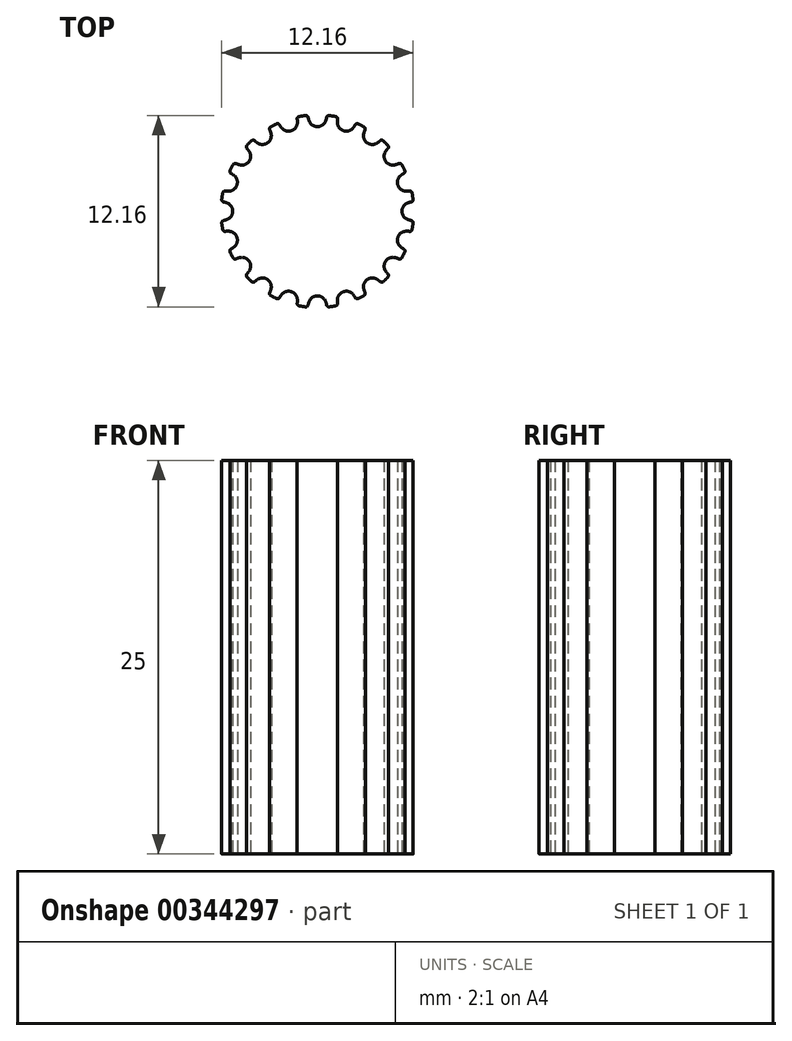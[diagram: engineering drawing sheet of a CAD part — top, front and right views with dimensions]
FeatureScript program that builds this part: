
annotation { "Feature Type Name" : "Feature", "Feature Type Description" : "" }
export const myFeature = defineFeature(function(context is Context, id is Id, definition is map)
    precondition{}
    {
        {
            var Q0;
            Q0=qCreatedBy(makeId("Top.planeOp"),FACE);
            var sketch = newSketch(context, id + "F0", { "sketchPlane" : qUnion([Q0])});
            skLineSegment(sketch, "E0", {"start": v(0, 6.12) * mm, "end": v(0, 6.37) * mm});
            skArc(sketch, "E1", {"start": v(-0.59, 5.95) * mm, "mid": v(-0.64, 6.05) * mm, "end": v(-0.75, 6.08) * mm});
            skArc(sketch, "E2", {"start": v(0.5, 5.7) * mm, "mid": v(0.56, 5.82) * mm, "end": v(0.59, 5.95) * mm});
            skLineSegment(sketch, "E3", {"start": v(0, 6.37) * mm, "end": v(0, 0) * mm, "construction": true});
            skCircle(sketch, "E4", {"center": v(0, 0) * mm, "radius": 6.12 * mm, "construction": true});
            skArc(sketch, "E5.trimOffspring", {"start": v(0.75, 6.08) * mm, "mid": v(0.64, 6.05) * mm, "end": v(0.59, 5.95) * mm});
            skArc(sketch, "E6.trimOffspring", {"start": v(-0.5, 5.7) * mm, "mid": v(0, 5.37) * mm, "end": v(0.5, 5.7) * mm});
            skArc(sketch, "E7.trimOffspring", {"start": v(-0.59, 5.95) * mm, "mid": v(-0.56, 5.82) * mm, "end": v(-0.5, 5.7) * mm});
            skPoint(sketch, "E8", {"position": v(0, 5.37) * mm});
            skCircle(sketch, "E9", {"center": v(0, 0) * mm, "radius": 6.37 * mm, "construction": true});
            skPoint(sketch, "E10", {"position": v(-0.96, 6.05) * mm});
            skPoint(sketch, "E11", {"position": v(0.96, 6.05) * mm});
            skArc(sketch, "E12", {"start": v(-0.75, 6.08) * mm, "mid": v(-0.86, 6.06) * mm, "end": v(-0.96, 6.05) * mm});
            skLineSegment(sketch, "E13", {"start": v(0, 0) * mm, "end": v(-1, 6.3) * mm, "construction": true});
            skLineSegment(sketch, "E14", {"start": v(0, 0) * mm, "end": v(1, 6.3) * mm, "construction": true});
            skArc(sketch, "E15", {"start": v(0.96, 6.05) * mm, "mid": v(0.86, 6.06) * mm, "end": v(0.75, 6.08) * mm});
            skLineSegment(sketch, "E16.1.0", {"start": v(0, 0) * mm, "end": v(0, 6.37) * mm, "construction": true});
            skLineSegment(sketch, "E17.2.3.0", {"start": v(0, 0) * mm, "end": v(-1.97, 6.06) * mm, "construction": true});
            skLineSegment(sketch, "E17.2.4.0", {"start": v(0, 0) * mm, "end": v(-2.9, 5.68) * mm, "construction": true});
            skLineSegment(sketch, "E17.2.5.0", {"start": v(0, 0) * mm, "end": v(-3.75, 5.16) * mm, "construction": true});
            skLineSegment(sketch, "E17.2.6.0", {"start": v(0, 0) * mm, "end": v(-4.5, 4.5) * mm, "construction": true});
            skLineSegment(sketch, "E17.2.7.0", {"start": v(0, 0) * mm, "end": v(-5.16, 3.75) * mm, "construction": true});
            skLineSegment(sketch, "E17.2.8.0", {"start": v(0, 0) * mm, "end": v(-5.68, 2.9) * mm, "construction": true});
            skLineSegment(sketch, "E17.2.9.0", {"start": v(0, 0) * mm, "end": v(-6.06, 1.97) * mm, "construction": true});
            skLineSegment(sketch, "E17.2.10.0", {"start": v(0, 0) * mm, "end": v(-6.3, 1) * mm, "construction": true});
            skLineSegment(sketch, "E17.2.11.0", {"start": v(0, 0) * mm, "end": v(-6.37, 0) * mm, "construction": true});
            skLineSegment(sketch, "E17.2.12.0", {"start": v(0, 0) * mm, "end": v(-6.3, -1) * mm, "construction": true});
            skLineSegment(sketch, "E17.2.13.0", {"start": v(0, 0) * mm, "end": v(-6.06, -1.97) * mm, "construction": true});
            skLineSegment(sketch, "E17.2.14.0", {"start": v(0, 0) * mm, "end": v(-5.68, -2.9) * mm, "construction": true});
            skLineSegment(sketch, "E17.2.15.0", {"start": v(0, 0) * mm, "end": v(-5.16, -3.75) * mm, "construction": true});
            skLineSegment(sketch, "E17.2.16.0", {"start": v(0, 0) * mm, "end": v(-4.5, -4.5) * mm, "construction": true});
            skLineSegment(sketch, "E17.2.17.0", {"start": v(0, 0) * mm, "end": v(-3.75, -5.16) * mm, "construction": true});
            skLineSegment(sketch, "E17.2.18.0", {"start": v(0, 0) * mm, "end": v(-2.9, -5.68) * mm, "construction": true});
            skLineSegment(sketch, "E17.2.19.0", {"start": v(0, 0) * mm, "end": v(-1.97, -6.06) * mm, "construction": true});
            skLineSegment(sketch, "E17.2.20.0", {"start": v(0, 0) * mm, "end": v(-1, -6.3) * mm, "construction": true});
            skLineSegment(sketch, "E17.2.21.0", {"start": v(0, 0) * mm, "end": v(0, -6.37) * mm, "construction": true});
            skLineSegment(sketch, "E17.2.22.0", {"start": v(0, 0) * mm, "end": v(1, -6.3) * mm, "construction": true});
            skLineSegment(sketch, "E17.2.23.0", {"start": v(0, 0) * mm, "end": v(1.97, -6.06) * mm, "construction": true});
            skLineSegment(sketch, "E18.2.24.0", {"start": v(0, 0) * mm, "end": v(2.9, -5.68) * mm, "construction": true});
            skLineSegment(sketch, "E18.2.25.0", {"start": v(0, 0) * mm, "end": v(3.75, -5.16) * mm, "construction": true});
            skLineSegment(sketch, "E18.2.26.0", {"start": v(0, 0) * mm, "end": v(4.5, -4.5) * mm, "construction": true});
            skLineSegment(sketch, "E18.2.27.0", {"start": v(0, 0) * mm, "end": v(5.16, -3.75) * mm, "construction": true});
            skLineSegment(sketch, "E18.2.28.0", {"start": v(0, 0) * mm, "end": v(5.68, -2.9) * mm, "construction": true});
            skLineSegment(sketch, "E18.2.29.0", {"start": v(0, 0) * mm, "end": v(6.06, -1.97) * mm, "construction": true});
            skLineSegment(sketch, "E18.2.30.0", {"start": v(0, 0) * mm, "end": v(6.3, -1) * mm, "construction": true});
            skLineSegment(sketch, "E18.2.31.0", {"start": v(0, 0) * mm, "end": v(6.37, 0) * mm, "construction": true});
            skLineSegment(sketch, "E18.2.32.0", {"start": v(0, 0) * mm, "end": v(6.3, 1) * mm, "construction": true});
            skLineSegment(sketch, "E18.2.33.0", {"start": v(0, 0) * mm, "end": v(6.06, 1.97) * mm, "construction": true});
            skLineSegment(sketch, "E18.2.34.0", {"start": v(0, 0) * mm, "end": v(5.68, 2.9) * mm, "construction": true});
            skLineSegment(sketch, "E18.2.35.0", {"start": v(0, 0) * mm, "end": v(5.16, 3.75) * mm, "construction": true});
            skLineSegment(sketch, "E18.2.36.0", {"start": v(0, 0) * mm, "end": v(4.5, 4.5) * mm, "construction": true});
            skLineSegment(sketch, "E18.2.37.0", {"start": v(0, 0) * mm, "end": v(3.75, 5.16) * mm, "construction": true});
            skLineSegment(sketch, "E18.2.38.0", {"start": v(0, 0) * mm, "end": v(2.9, 5.68) * mm, "construction": true});
            skLineSegment(sketch, "E18.2.39.0", {"start": v(0, 0) * mm, "end": v(1.97, 6.06) * mm, "construction": true});
            skArc(sketch, "E19.1.0", {"start": v(-2.6, 5.55) * mm, "mid": v(-2.69, 5.5) * mm, "end": v(-2.78, 5.46) * mm});
            skArc(sketch, "E19.1.1", {"start": v(-2.4, 5.48) * mm, "mid": v(-2.48, 5.55) * mm, "end": v(-2.6, 5.55) * mm});
            skArc(sketch, "E19.1.2", {"start": v(-2.4, 5.48) * mm, "mid": v(-2.33, 5.37) * mm, "end": v(-2.25, 5.26) * mm});
            skArc(sketch, "E19.1.3", {"start": v(-2.25, 5.26) * mm, "mid": v(-1.66, 5.1) * mm, "end": v(-1.28, 5.58) * mm});
            skArc(sketch, "E19.1.4", {"start": v(-1.28, 5.58) * mm, "mid": v(-1.27, 5.71) * mm, "end": v(-1.28, 5.84) * mm});
            skArc(sketch, "E19.1.5", {"start": v(-1.16, 6.01) * mm, "mid": v(-1.26, 5.95) * mm, "end": v(-1.28, 5.84) * mm});
            skArc(sketch, "E19.1.6", {"start": v(-0.96, 6.05) * mm, "mid": v(-1.06, 6.03) * mm, "end": v(-1.16, 6.01) * mm});
            skArc(sketch, "E19.2.0", {"start": v(-4.18, 4.47) * mm, "mid": v(-4.26, 4.4) * mm, "end": v(-4.33, 4.33) * mm});
            skArc(sketch, "E19.2.1", {"start": v(-3.97, 4.47) * mm, "mid": v(-4.08, 4.51) * mm, "end": v(-4.18, 4.47) * mm});
            skArc(sketch, "E19.2.2", {"start": v(-3.97, 4.47) * mm, "mid": v(-3.87, 4.38) * mm, "end": v(-3.76, 4.31) * mm});
            skArc(sketch, "E19.2.3", {"start": v(-3.76, 4.31) * mm, "mid": v(-3.16, 4.35) * mm, "end": v(-2.94, 4.91) * mm});
            skArc(sketch, "E19.2.4", {"start": v(-2.94, 4.91) * mm, "mid": v(-2.97, 5.04) * mm, "end": v(-3.02, 5.16) * mm});
            skArc(sketch, "E19.2.5", {"start": v(-2.96, 5.36) * mm, "mid": v(-3.03, 5.27) * mm, "end": v(-3.02, 5.16) * mm});
            skArc(sketch, "E19.2.6", {"start": v(-2.78, 5.46) * mm, "mid": v(-2.87, 5.4) * mm, "end": v(-2.96, 5.36) * mm});
            skArc(sketch, "E20.3.3.0", {"start": v(-5.36, 2.96) * mm, "mid": v(-5.4, 2.87) * mm, "end": v(-5.46, 2.78) * mm});
            skArc(sketch, "E20.4.3.0", {"start": v(-5.16, 3.02) * mm, "mid": v(-5.27, 3.03) * mm, "end": v(-5.36, 2.96) * mm});
            skArc(sketch, "E20.8.3.0", {"start": v(-5.16, 3.02) * mm, "mid": v(-5.04, 2.97) * mm, "end": v(-4.91, 2.94) * mm});
            skArc(sketch, "E20.12.3.0", {"start": v(-4.91, 2.94) * mm, "mid": v(-4.35, 3.16) * mm, "end": v(-4.31, 3.76) * mm});
            skArc(sketch, "E20.16.3.0", {"start": v(-4.31, 3.76) * mm, "mid": v(-4.38, 3.87) * mm, "end": v(-4.47, 3.97) * mm});
            skArc(sketch, "E20.20.3.0", {"start": v(-4.47, 4.18) * mm, "mid": v(-4.51, 4.08) * mm, "end": v(-4.47, 3.97) * mm});
            skArc(sketch, "E20.24.3.0", {"start": v(-4.33, 4.33) * mm, "mid": v(-4.4, 4.26) * mm, "end": v(-4.47, 4.18) * mm});
            skArc(sketch, "E20.3.4.0", {"start": v(-6.01, 1.16) * mm, "mid": v(-6.03, 1.06) * mm, "end": v(-6.05, 0.96) * mm});
            skArc(sketch, "E20.4.4.0", {"start": v(-5.84, 1.28) * mm, "mid": v(-5.95, 1.26) * mm, "end": v(-6.01, 1.16) * mm});
            skArc(sketch, "E20.8.4.0", {"start": v(-5.84, 1.28) * mm, "mid": v(-5.71, 1.27) * mm, "end": v(-5.58, 1.28) * mm});
            skArc(sketch, "E20.12.4.0", {"start": v(-5.58, 1.28) * mm, "mid": v(-5.1, 1.66) * mm, "end": v(-5.26, 2.25) * mm});
            skArc(sketch, "E20.16.4.0", {"start": v(-5.26, 2.25) * mm, "mid": v(-5.37, 2.33) * mm, "end": v(-5.48, 2.4) * mm});
            skArc(sketch, "E20.20.4.0", {"start": v(-5.55, 2.6) * mm, "mid": v(-5.55, 2.48) * mm, "end": v(-5.48, 2.4) * mm});
            skArc(sketch, "E20.24.4.0", {"start": v(-5.46, 2.78) * mm, "mid": v(-5.5, 2.69) * mm, "end": v(-5.55, 2.6) * mm});
            skArc(sketch, "E20.3.5.0", {"start": v(-6.08, -0.75) * mm, "mid": v(-6.06, -0.86) * mm, "end": v(-6.05, -0.96) * mm});
            skArc(sketch, "E20.4.5.0", {"start": v(-5.95, -0.59) * mm, "mid": v(-6.05, -0.64) * mm, "end": v(-6.08, -0.75) * mm});
            skArc(sketch, "E20.8.5.0", {"start": v(-5.95, -0.59) * mm, "mid": v(-5.82, -0.56) * mm, "end": v(-5.7, -0.5) * mm});
            skArc(sketch, "E20.12.5.0", {"start": v(-5.7, -0.5) * mm, "mid": v(-5.37, 0) * mm, "end": v(-5.7, 0.5) * mm});
            skArc(sketch, "E20.16.5.0", {"start": v(-5.7, 0.5) * mm, "mid": v(-5.82, 0.56) * mm, "end": v(-5.95, 0.59) * mm});
            skArc(sketch, "E20.20.5.0", {"start": v(-6.08, 0.75) * mm, "mid": v(-6.05, 0.64) * mm, "end": v(-5.95, 0.59) * mm});
            skArc(sketch, "E20.24.5.0", {"start": v(-6.05, 0.96) * mm, "mid": v(-6.06, 0.86) * mm, "end": v(-6.08, 0.75) * mm});
            skArc(sketch, "E20.3.6.0", {"start": v(-5.55, -2.6) * mm, "mid": v(-5.5, -2.69) * mm, "end": v(-5.46, -2.78) * mm});
            skArc(sketch, "E20.4.6.0", {"start": v(-5.48, -2.4) * mm, "mid": v(-5.55, -2.48) * mm, "end": v(-5.55, -2.6) * mm});
            skArc(sketch, "E20.8.6.0", {"start": v(-5.48, -2.4) * mm, "mid": v(-5.37, -2.33) * mm, "end": v(-5.26, -2.25) * mm});
            skArc(sketch, "E20.12.6.0", {"start": v(-5.26, -2.25) * mm, "mid": v(-5.1, -1.66) * mm, "end": v(-5.58, -1.28) * mm});
            skArc(sketch, "E20.16.6.0", {"start": v(-5.58, -1.28) * mm, "mid": v(-5.71, -1.27) * mm, "end": v(-5.84, -1.28) * mm});
            skArc(sketch, "E20.20.6.0", {"start": v(-6.01, -1.16) * mm, "mid": v(-5.95, -1.26) * mm, "end": v(-5.84, -1.28) * mm});
            skArc(sketch, "E20.24.6.0", {"start": v(-6.05, -0.96) * mm, "mid": v(-6.03, -1.06) * mm, "end": v(-6.01, -1.16) * mm});
            skArc(sketch, "E20.3.7.0", {"start": v(-4.47, -4.18) * mm, "mid": v(-4.4, -4.26) * mm, "end": v(-4.33, -4.33) * mm});
            skArc(sketch, "E20.4.7.0", {"start": v(-4.47, -3.97) * mm, "mid": v(-4.51, -4.08) * mm, "end": v(-4.47, -4.18) * mm});
            skArc(sketch, "E20.8.7.0", {"start": v(-4.47, -3.97) * mm, "mid": v(-4.38, -3.87) * mm, "end": v(-4.31, -3.76) * mm});
            skArc(sketch, "E20.12.7.0", {"start": v(-4.31, -3.76) * mm, "mid": v(-4.35, -3.16) * mm, "end": v(-4.91, -2.94) * mm});
            skArc(sketch, "E20.16.7.0", {"start": v(-4.91, -2.94) * mm, "mid": v(-5.04, -2.97) * mm, "end": v(-5.16, -3.02) * mm});
            skArc(sketch, "E20.20.7.0", {"start": v(-5.36, -2.96) * mm, "mid": v(-5.27, -3.03) * mm, "end": v(-5.16, -3.02) * mm});
            skArc(sketch, "E20.24.7.0", {"start": v(-5.46, -2.78) * mm, "mid": v(-5.4, -2.87) * mm, "end": v(-5.36, -2.96) * mm});
            skArc(sketch, "E20.3.8.0", {"start": v(-2.96, -5.36) * mm, "mid": v(-2.87, -5.4) * mm, "end": v(-2.78, -5.46) * mm});
            skArc(sketch, "E20.4.8.0", {"start": v(-3.02, -5.16) * mm, "mid": v(-3.03, -5.27) * mm, "end": v(-2.96, -5.36) * mm});
            skArc(sketch, "E20.8.8.0", {"start": v(-3.02, -5.16) * mm, "mid": v(-2.97, -5.04) * mm, "end": v(-2.94, -4.91) * mm});
            skArc(sketch, "E20.12.8.0", {"start": v(-2.94, -4.91) * mm, "mid": v(-3.16, -4.35) * mm, "end": v(-3.76, -4.31) * mm});
            skArc(sketch, "E20.16.8.0", {"start": v(-3.76, -4.31) * mm, "mid": v(-3.87, -4.38) * mm, "end": v(-3.97, -4.47) * mm});
            skArc(sketch, "E20.20.8.0", {"start": v(-4.18, -4.47) * mm, "mid": v(-4.08, -4.51) * mm, "end": v(-3.97, -4.47) * mm});
            skArc(sketch, "E20.24.8.0", {"start": v(-4.33, -4.33) * mm, "mid": v(-4.26, -4.4) * mm, "end": v(-4.18, -4.47) * mm});
            skArc(sketch, "E20.3.9.0", {"start": v(-1.16, -6.01) * mm, "mid": v(-1.06, -6.03) * mm, "end": v(-0.96, -6.05) * mm});
            skArc(sketch, "E20.4.9.0", {"start": v(-1.28, -5.84) * mm, "mid": v(-1.26, -5.95) * mm, "end": v(-1.16, -6.01) * mm});
            skArc(sketch, "E20.8.9.0", {"start": v(-1.28, -5.84) * mm, "mid": v(-1.27, -5.71) * mm, "end": v(-1.28, -5.58) * mm});
            skArc(sketch, "E20.12.9.0", {"start": v(-1.28, -5.58) * mm, "mid": v(-1.66, -5.1) * mm, "end": v(-2.25, -5.26) * mm});
            skArc(sketch, "E20.16.9.0", {"start": v(-2.25, -5.26) * mm, "mid": v(-2.33, -5.37) * mm, "end": v(-2.4, -5.48) * mm});
            skArc(sketch, "E20.20.9.0", {"start": v(-2.6, -5.55) * mm, "mid": v(-2.48, -5.55) * mm, "end": v(-2.4, -5.48) * mm});
            skArc(sketch, "E20.24.9.0", {"start": v(-2.78, -5.46) * mm, "mid": v(-2.69, -5.5) * mm, "end": v(-2.6, -5.55) * mm});
            skArc(sketch, "E20.3.10.0", {"start": v(0.75, -6.08) * mm, "mid": v(0.86, -6.06) * mm, "end": v(0.96, -6.05) * mm});
            skArc(sketch, "E20.4.10.0", {"start": v(0.59, -5.95) * mm, "mid": v(0.64, -6.05) * mm, "end": v(0.75, -6.08) * mm});
            skArc(sketch, "E20.8.10.0", {"start": v(0.59, -5.95) * mm, "mid": v(0.56, -5.82) * mm, "end": v(0.5, -5.7) * mm});
            skArc(sketch, "E20.12.10.0", {"start": v(0.5, -5.7) * mm, "mid": v(0, -5.37) * mm, "end": v(-0.5, -5.7) * mm});
            skArc(sketch, "E20.16.10.0", {"start": v(-0.5, -5.7) * mm, "mid": v(-0.56, -5.82) * mm, "end": v(-0.59, -5.95) * mm});
            skArc(sketch, "E20.20.10.0", {"start": v(-0.75, -6.08) * mm, "mid": v(-0.64, -6.05) * mm, "end": v(-0.59, -5.95) * mm});
            skArc(sketch, "E20.24.10.0", {"start": v(-0.96, -6.05) * mm, "mid": v(-0.86, -6.06) * mm, "end": v(-0.75, -6.08) * mm});
            skArc(sketch, "E20.3.11.0", {"start": v(2.6, -5.55) * mm, "mid": v(2.69, -5.5) * mm, "end": v(2.78, -5.46) * mm});
            skArc(sketch, "E20.4.11.0", {"start": v(2.4, -5.48) * mm, "mid": v(2.48, -5.55) * mm, "end": v(2.6, -5.55) * mm});
            skArc(sketch, "E20.8.11.0", {"start": v(2.4, -5.48) * mm, "mid": v(2.33, -5.37) * mm, "end": v(2.25, -5.26) * mm});
            skArc(sketch, "E20.12.11.0", {"start": v(2.25, -5.26) * mm, "mid": v(1.66, -5.1) * mm, "end": v(1.28, -5.58) * mm});
            skArc(sketch, "E20.16.11.0", {"start": v(1.28, -5.58) * mm, "mid": v(1.27, -5.71) * mm, "end": v(1.28, -5.84) * mm});
            skArc(sketch, "E20.20.11.0", {"start": v(1.16, -6.01) * mm, "mid": v(1.26, -5.95) * mm, "end": v(1.28, -5.84) * mm});
            skArc(sketch, "E20.24.11.0", {"start": v(0.96, -6.05) * mm, "mid": v(1.06, -6.03) * mm, "end": v(1.16, -6.01) * mm});
            skArc(sketch, "E20.3.12.0", {"start": v(4.18, -4.47) * mm, "mid": v(4.26, -4.4) * mm, "end": v(4.33, -4.33) * mm});
            skArc(sketch, "E20.4.12.0", {"start": v(3.97, -4.47) * mm, "mid": v(4.08, -4.51) * mm, "end": v(4.18, -4.47) * mm});
            skArc(sketch, "E20.8.12.0", {"start": v(3.97, -4.47) * mm, "mid": v(3.87, -4.38) * mm, "end": v(3.76, -4.31) * mm});
            skArc(sketch, "E20.12.12.0", {"start": v(3.76, -4.31) * mm, "mid": v(3.16, -4.35) * mm, "end": v(2.94, -4.91) * mm});
            skArc(sketch, "E20.16.12.0", {"start": v(2.94, -4.91) * mm, "mid": v(2.97, -5.04) * mm, "end": v(3.02, -5.16) * mm});
            skArc(sketch, "E20.20.12.0", {"start": v(2.96, -5.36) * mm, "mid": v(3.03, -5.27) * mm, "end": v(3.02, -5.16) * mm});
            skArc(sketch, "E20.24.12.0", {"start": v(2.78, -5.46) * mm, "mid": v(2.87, -5.4) * mm, "end": v(2.96, -5.36) * mm});
            skArc(sketch, "E20.3.13.0", {"start": v(5.36, -2.96) * mm, "mid": v(5.4, -2.87) * mm, "end": v(5.46, -2.78) * mm});
            skArc(sketch, "E20.4.13.0", {"start": v(5.16, -3.02) * mm, "mid": v(5.27, -3.03) * mm, "end": v(5.36, -2.96) * mm});
            skArc(sketch, "E20.8.13.0", {"start": v(5.16, -3.02) * mm, "mid": v(5.04, -2.97) * mm, "end": v(4.91, -2.94) * mm});
            skArc(sketch, "E20.12.13.0", {"start": v(4.91, -2.94) * mm, "mid": v(4.35, -3.16) * mm, "end": v(4.31, -3.76) * mm});
            skArc(sketch, "E20.16.13.0", {"start": v(4.31, -3.76) * mm, "mid": v(4.38, -3.87) * mm, "end": v(4.47, -3.97) * mm});
            skArc(sketch, "E20.20.13.0", {"start": v(4.47, -4.18) * mm, "mid": v(4.51, -4.08) * mm, "end": v(4.47, -3.97) * mm});
            skArc(sketch, "E20.24.13.0", {"start": v(4.33, -4.33) * mm, "mid": v(4.4, -4.26) * mm, "end": v(4.47, -4.18) * mm});
            skArc(sketch, "E20.3.14.0", {"start": v(6.01, -1.16) * mm, "mid": v(6.03, -1.06) * mm, "end": v(6.05, -0.96) * mm});
            skArc(sketch, "E20.4.14.0", {"start": v(5.84, -1.28) * mm, "mid": v(5.95, -1.26) * mm, "end": v(6.01, -1.16) * mm});
            skArc(sketch, "E20.8.14.0", {"start": v(5.84, -1.28) * mm, "mid": v(5.71, -1.27) * mm, "end": v(5.58, -1.28) * mm});
            skArc(sketch, "E20.12.14.0", {"start": v(5.58, -1.28) * mm, "mid": v(5.1, -1.66) * mm, "end": v(5.26, -2.25) * mm});
            skArc(sketch, "E20.16.14.0", {"start": v(5.26, -2.25) * mm, "mid": v(5.37, -2.33) * mm, "end": v(5.48, -2.4) * mm});
            skArc(sketch, "E20.20.14.0", {"start": v(5.55, -2.6) * mm, "mid": v(5.55, -2.48) * mm, "end": v(5.48, -2.4) * mm});
            skArc(sketch, "E20.24.14.0", {"start": v(5.46, -2.78) * mm, "mid": v(5.5, -2.69) * mm, "end": v(5.55, -2.6) * mm});
            skArc(sketch, "E20.3.15.0", {"start": v(6.08, 0.75) * mm, "mid": v(6.06, 0.86) * mm, "end": v(6.05, 0.96) * mm});
            skArc(sketch, "E20.4.15.0", {"start": v(5.95, 0.59) * mm, "mid": v(6.05, 0.64) * mm, "end": v(6.08, 0.75) * mm});
            skArc(sketch, "E20.8.15.0", {"start": v(5.95, 0.59) * mm, "mid": v(5.82, 0.56) * mm, "end": v(5.7, 0.5) * mm});
            skArc(sketch, "E20.12.15.0", {"start": v(5.7, 0.5) * mm, "mid": v(5.37, 0) * mm, "end": v(5.7, -0.5) * mm});
            skArc(sketch, "E20.16.15.0", {"start": v(5.7, -0.5) * mm, "mid": v(5.82, -0.56) * mm, "end": v(5.95, -0.59) * mm});
            skArc(sketch, "E20.20.15.0", {"start": v(6.08, -0.75) * mm, "mid": v(6.05, -0.64) * mm, "end": v(5.95, -0.59) * mm});
            skArc(sketch, "E20.24.15.0", {"start": v(6.05, -0.96) * mm, "mid": v(6.06, -0.86) * mm, "end": v(6.08, -0.75) * mm});
            skArc(sketch, "E20.3.16.0", {"start": v(5.55, 2.6) * mm, "mid": v(5.5, 2.69) * mm, "end": v(5.46, 2.78) * mm});
            skArc(sketch, "E20.4.16.0", {"start": v(5.48, 2.4) * mm, "mid": v(5.55, 2.48) * mm, "end": v(5.55, 2.6) * mm});
            skArc(sketch, "E20.8.16.0", {"start": v(5.48, 2.4) * mm, "mid": v(5.37, 2.33) * mm, "end": v(5.26, 2.25) * mm});
            skArc(sketch, "E20.12.16.0", {"start": v(5.26, 2.25) * mm, "mid": v(5.1, 1.66) * mm, "end": v(5.58, 1.28) * mm});
            skArc(sketch, "E20.16.16.0", {"start": v(5.58, 1.28) * mm, "mid": v(5.71, 1.27) * mm, "end": v(5.84, 1.28) * mm});
            skArc(sketch, "E20.20.16.0", {"start": v(6.01, 1.16) * mm, "mid": v(5.95, 1.26) * mm, "end": v(5.84, 1.28) * mm});
            skArc(sketch, "E20.24.16.0", {"start": v(6.05, 0.96) * mm, "mid": v(6.03, 1.06) * mm, "end": v(6.01, 1.16) * mm});
            skArc(sketch, "E20.3.17.0", {"start": v(4.47, 4.18) * mm, "mid": v(4.4, 4.26) * mm, "end": v(4.33, 4.33) * mm});
            skArc(sketch, "E20.4.17.0", {"start": v(4.47, 3.97) * mm, "mid": v(4.51, 4.08) * mm, "end": v(4.47, 4.18) * mm});
            skArc(sketch, "E20.8.17.0", {"start": v(4.47, 3.97) * mm, "mid": v(4.38, 3.87) * mm, "end": v(4.31, 3.76) * mm});
            skArc(sketch, "E20.12.17.0", {"start": v(4.31, 3.76) * mm, "mid": v(4.35, 3.16) * mm, "end": v(4.91, 2.94) * mm});
            skArc(sketch, "E20.16.17.0", {"start": v(4.91, 2.94) * mm, "mid": v(5.04, 2.97) * mm, "end": v(5.16, 3.02) * mm});
            skArc(sketch, "E20.20.17.0", {"start": v(5.36, 2.96) * mm, "mid": v(5.27, 3.03) * mm, "end": v(5.16, 3.02) * mm});
            skArc(sketch, "E20.24.17.0", {"start": v(5.46, 2.78) * mm, "mid": v(5.4, 2.87) * mm, "end": v(5.36, 2.96) * mm});
            skArc(sketch, "E20.3.18.0", {"start": v(2.96, 5.36) * mm, "mid": v(2.87, 5.4) * mm, "end": v(2.78, 5.46) * mm});
            skArc(sketch, "E20.4.18.0", {"start": v(3.02, 5.16) * mm, "mid": v(3.03, 5.27) * mm, "end": v(2.96, 5.36) * mm});
            skArc(sketch, "E20.8.18.0", {"start": v(3.02, 5.16) * mm, "mid": v(2.97, 5.04) * mm, "end": v(2.94, 4.91) * mm});
            skArc(sketch, "E20.12.18.0", {"start": v(2.94, 4.91) * mm, "mid": v(3.16, 4.35) * mm, "end": v(3.76, 4.31) * mm});
            skArc(sketch, "E20.16.18.0", {"start": v(3.76, 4.31) * mm, "mid": v(3.87, 4.38) * mm, "end": v(3.97, 4.47) * mm});
            skArc(sketch, "E20.20.18.0", {"start": v(4.18, 4.47) * mm, "mid": v(4.08, 4.51) * mm, "end": v(3.97, 4.47) * mm});
            skArc(sketch, "E20.24.18.0", {"start": v(4.33, 4.33) * mm, "mid": v(4.26, 4.4) * mm, "end": v(4.18, 4.47) * mm});
            skArc(sketch, "E20.3.19.0", {"start": v(1.16, 6.01) * mm, "mid": v(1.06, 6.03) * mm, "end": v(0.96, 6.05) * mm});
            skArc(sketch, "E20.4.19.0", {"start": v(1.28, 5.84) * mm, "mid": v(1.26, 5.95) * mm, "end": v(1.16, 6.01) * mm});
            skArc(sketch, "E20.8.19.0", {"start": v(1.28, 5.84) * mm, "mid": v(1.27, 5.71) * mm, "end": v(1.28, 5.58) * mm});
            skArc(sketch, "E20.12.19.0", {"start": v(1.28, 5.58) * mm, "mid": v(1.66, 5.1) * mm, "end": v(2.25, 5.26) * mm});
            skArc(sketch, "E20.16.19.0", {"start": v(2.25, 5.26) * mm, "mid": v(2.33, 5.37) * mm, "end": v(2.4, 5.48) * mm});
            skArc(sketch, "E20.20.19.0", {"start": v(2.6, 5.55) * mm, "mid": v(2.48, 5.55) * mm, "end": v(2.4, 5.48) * mm});
            skArc(sketch, "E20.24.19.0", {"start": v(2.78, 5.46) * mm, "mid": v(2.69, 5.5) * mm, "end": v(2.6, 5.55) * mm});
            skSolve(sketch);
        }
        {
            var Q0;
            Q0=makeQuery(id+"F0.imprint","IMPRINT",FACE,{"disambiguationData":[TD([[makeQuery(id+"F0.imprint","IMPRINT",EDGE,{"derivedFrom":sQuery(id+"F0.wireOp",EDGE,"E1")}),1.0]])]});
            extrude(context, id + "F1", {"entities" : qUnion([Q0]), "depth" : 25 * mm});
        }
    });
